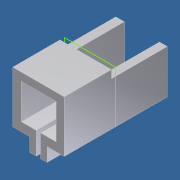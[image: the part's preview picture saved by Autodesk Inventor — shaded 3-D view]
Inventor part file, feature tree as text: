
AUTODESK INVENTOR PART (.ipt)
format: ipt  version: unknown  size: 322,560 bytes
history: native  units: in
note: dims shown in document units (in); Inventor stores cm internally (conversion verified against a paired STEP export)
features: sketch x13, extrude x11
ambient origin geometry x8: Origin, YZ Plane, XZ Plane, XY Plane, X Axis, Y Axis, Z Axis, Center Point
bodies: Solid1 (feature_tree)
feature tree (24):
  extrude  "Extrusion1"  Depth=0.5in TaperAngle=0.0deg
  extrude  "Extrusion6"  Depth=1.5in TaperAngle=0.0deg
  sketch  "Sketch8"  dims[d66=1.5in d67=0.0in d73=0.062in]
  sketch  "Sketch9"  dims[d77=0.4in d78=0.0in d82=0.2in]
  extrude  "Extrusion10"  Depth=0.062in
  extrude  "Extrusion11"  Depth=0.2in
  extrude  "Extrusion12"  Depth=1.16in
  sketch  "Sketch17"  dims[d90=1.1523in d91=0.23in d92=0.0in]
  extrude  "Extrusion14"  Depth=0.159in
  extrude  "Extrusion16"  Depth=1.0in TaperAngle=0.0deg
  extrude  "Extrusion17"  Depth=0.23in TaperAngle=0.0deg
  extrude  "Extrusion18"  Depth=3.0in TaperAngle=0.0deg
  extrude  "Extrusion19"  [1 undecoded]
  extrude  "Extrusion20"  [1 undecoded]
  sketch  "Sketch1"  dims[d6=1.5in d7=0.0in d37=0.5in d38=0.0in]
  sketch  "Sketch7"  dims[d62=2.0in d63=0.0in d64=1.5in d65=0.0in]
  sketch  "Sketch11"  dims[d83=1.16in d84=1.16in]
  sketch  "Sketch15"  dims[d85=0.159in d86=0.159in]
  sketch  "Sketch16"  dims[d87=0.159in d88=1.0in d89=0.0in]
  sketch  "Sketch19"  dims[d93=2.0in d94=0.0in d95=3.0in d96=0.0in]
  sketch  "Sketch21"  dims[d97=0.471in d98=0.0in]
  sketch  "Sketch22"
  sketch  "Sketch23"
  sketch  "Sketch24"
note: 2 required parameter values undecoded (feature->parameter linkage not recoverable at this tier; creation-order binding heuristic only, values carry confidence <= 0.55)
